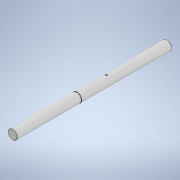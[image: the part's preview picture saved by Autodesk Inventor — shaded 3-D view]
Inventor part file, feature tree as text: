
AUTODESK INVENTOR PART (.ipt)
format: ipt  version: 2022 (Build 260153000, 153)  size: 125,440 bytes
history: native  units: mm
features: sketch x2, other x1, hole x1, extrude x1, projected_geometry x1
ambient origin geometry x8: Origin, YZ Plane, XZ Plane, XY Plane, X Axis, Y Axis, Z Axis, Center Point
bodies: Solid1 (feature_tree)
feature tree (6):
  other  "Shaft"
  hole  "Hole for pin"  [1 undecoded]
  extrude  "Pinhole"  Depth=0.5mm
  sketch  "Sketch1"  dims[d0=120.0mm d2=1.5mm]
  sketch  "Sketch2"  dims[d3=0.5mm d4=0.5mm d5=135.0deg d6=9.0mm d8=170.0mm d9=1.414mm d10=8.0mm d11=90.0deg d12=9.0mm d13=50.0mm d14=3.5mm d15=5.0mm d16=0.0mm d17=0.0mm]
  projected_geometry  "Projected Loop1"
note: 1 required parameter value undecoded (feature->parameter linkage not recoverable at this tier; creation-order binding heuristic only, values carry confidence <= 0.55)
